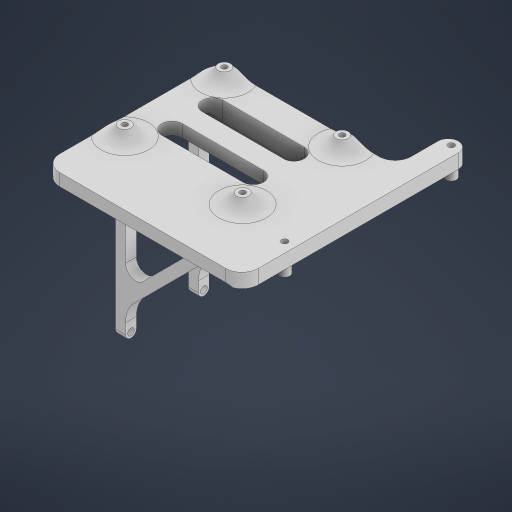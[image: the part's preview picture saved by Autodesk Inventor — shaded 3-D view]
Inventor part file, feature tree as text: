
AUTODESK INVENTOR PART (.ipt)
format: ipt  version: 2024.1 (Build 281209000, 209)  size: 777,216 bytes
history: native  units: mm
features: extrude x29, sketch x28, projected_geometry x23, fillet x11, other x1, chamfer x1
ambient origin geometry x8: Origin, YZ Plane, XZ Plane, XY Plane, X Axis, Y Axis, Z Axis, Center Point
bodies: Body1 (feature_tree)
feature tree (93):
  other  "솔리드1"
  extrude  "돌출1"  Depth=3.0mm
  extrude  "돌출2"  Depth=1.0mm
  extrude  "돌출4"  Depth=81.4mm TaperAngle=0.0deg
  extrude  "돌출5"  Depth=5.0mm
  extrude  "돌출6"  Depth=5.0mm
  extrude  "돌출7"  Depth=1.0mm
  extrude  "돌출8"  Depth=1.0mm TaperAngle=0.0deg
  extrude  "돌출9"  Depth=5.0mm
  extrude  "돌출10"  Depth=1.0mm
  extrude  "돌출11"  Depth=2.0mm TaperAngle=0.0deg
  extrude  "돌출12"  Depth=1.0mm TaperAngle=0.0deg
  extrude  "돌출13"  Depth=1.0mm TaperAngle=0.0deg
  extrude  "돌출14"  Depth=5.0mm
  fillet  "모깎기1"  Radius=1.0mm
  extrude  "돌출15"  Depth=1.0mm TaperAngle=0.0deg
  extrude  "돌출16"  Depth=1.0mm TaperAngle=0.0deg
  chamfer  "모따기1"  Distance=79.4mm
  extrude  "돌출17"  Depth=79.4mm TaperAngle=0.0deg
  fillet  "모깎기2"  Radius=10.0mm
  extrude  "돌출18"  Depth=1.0mm
  fillet  "모깎기4"  Radius=33.05mm
  extrude  "돌출19"  Depth=92.7mm TaperAngle=0.0deg
  extrude  "돌출20"  Depth=10.0mm
  extrude  "돌출21"  Depth=1.0mm
  sketch  "스케치23"
  extrude  "돌출22"  Depth=5.0mm TaperAngle=0.0deg
  extrude  "돌출23"  Depth=1.0mm TaperAngle=0.0deg
  sketch  "스케치24"
  extrude  "돌출24"  Depth=1.0mm
  extrude  "돌출26"  Depth=2.35mm
  extrude  "돌출27"  Depth=5.3mm
  fillet  "모깎기5"  Radius=85.05mm
  fillet  "모깎기6"  Radius=3.3mm
  fillet  "모깎기7"  Radius=2.65mm
  extrude  "돌출28"  Depth=2.65mm
  extrude  "돌출29"  Depth=85.05mm TaperAngle=0.0deg
  extrude  "돌출30"  Depth=2.65mm
  extrude  "돌출31"  Depth=10.0mm
  fillet  "모깎기8"  Radius=1.0mm
  fillet  "모깎기9"  Radius=25.9mm
  fillet  "모깎기10"  Radius=1.0mm
  fillet  "모깎기11"  Radius=5.3mm
  fillet  "모깎기12"  Radius=10.0mm
  sketch  "스케치1"
  sketch  "스케치2"
  projected_geometry  "투영된 루프1"
  sketch  "스케치4"
  sketch  "스케치6"
  projected_geometry  "투영된 루프2"
  sketch  "스케치7"
  projected_geometry  "투영된 루프3"
  sketch  "스케치8"
  sketch  "스케치9"
  projected_geometry  "투영된 루프4"
  projected_geometry  "투영된 루프5"
  sketch  "스케치10"
  sketch  "스케치11"
  sketch  "스케치12"
  sketch  "스케치13"
  projected_geometry  "투영된 루프6"
  projected_geometry  "투영된 루프7"
  sketch  "스케치14"
  sketch  "스케치15"
  sketch  "스케치16"
  projected_geometry  "투영된 루프8"
  sketch  "스케치17"
  projected_geometry  "투영된 루프9"
  sketch  "스케치18"
  projected_geometry  "투영된 루프10"
  sketch  "스케치19"
  sketch  "스케치20"
  sketch  "스케치21"
  sketch  "스케치22"
  projected_geometry  "투영된 루프11"
  projected_geometry  "투영된 루프12"
  projected_geometry  "투영된 루프13"
  projected_geometry  "투영된 루프14"
  projected_geometry  "투영된 루프15"
  sketch  "스케치25"
  projected_geometry  "투영된 루프16"
  projected_geometry  "투영된 루프17"
  sketch  "스케치26"
  projected_geometry  "투영된 루프18"
  projected_geometry  "투영된 루프19"
  sketch  "스케치27"
  projected_geometry  "투영된 루프20"
  sketch  "스케치28"
  projected_geometry  "투영된 루프21"
  sketch  "스케치29"
  projected_geometry  "투영된 루프22"
  sketch  "스케치30"
  projected_geometry  "투영된 루프23"
